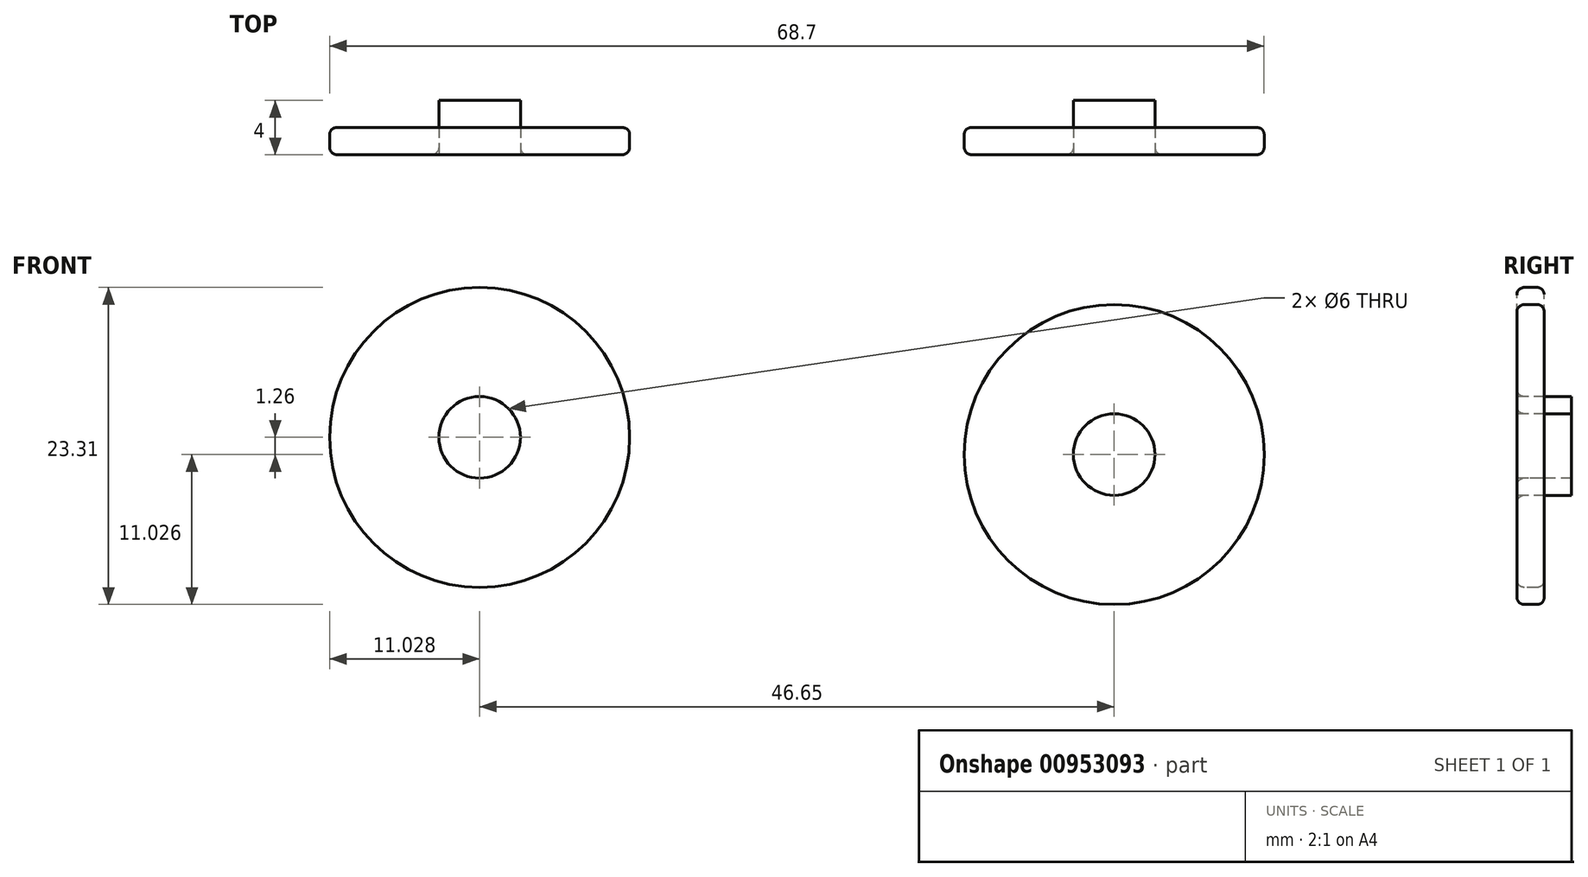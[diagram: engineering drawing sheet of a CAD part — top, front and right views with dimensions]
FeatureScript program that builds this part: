
annotation { "Feature Type Name" : "Feature", "Feature Type Description" : "" }
export const myFeature = defineFeature(function(context is Context, id is Id, definition is map)
    precondition{}
    {
        {
            var Q0;
            Q0=qCreatedBy(makeId("Front.planeOp"),FACE);
            var sketch = newSketch(context, id + "F0", { "sketchPlane" : qUnion([Q0])});
            skCircle(sketch, "E0", {"center": v(-66.5, 54.88) * mm, "radius": 11.03 * mm});
            skCircle(sketch, "E1", {"center": v(-19.84, 53.62) * mm, "radius": 11.03 * mm});
            skCircle(sketch, "E2", {"center": v(-66.5, 54.88) * mm, "radius": 3 * mm});
            skCircle(sketch, "E3", {"center": v(-19.84, 53.62) * mm, "radius": 3 * mm});
            skSolve(sketch);
        }
        {
            var Q0;
            Q0=makeQuery(id+"F0.imprint","IMPRINT",FACE,{"disambiguationData":[TD([[makeQuery(id+"F0.imprint","IMPRINT",EDGE,{"derivedFrom":sQuery(id+"F0.wireOp",EDGE,"E1")}),1.0]])]});
            var Q1;
            Q1=makeQuery(id+"F0.imprint","IMPRINT",FACE,{"disambiguationData":[TD([[makeQuery(id+"F0.imprint","IMPRINT",EDGE,{"derivedFrom":sQuery(id+"F0.wireOp",EDGE,"E0")}),1.0]])]});
            extrude(context, id + "F1", {"entities" : qUnion([Q0, Q1]), "depth" : -2 * mm, "offsetDistance" : 25.4 * mm});
        }
        {
            var Q0;
            Q0=makeQuery(id+"F1.opExtrude","CAP_EDGE",EDGE,{"disambiguationData":[OSD([sQuery(id+"F0.wireOp",EDGE,"E1")])],"isStart":false});
            var Q1;
            Q1=makeQuery(id+"F1.opExtrude","CAP_EDGE",EDGE,{"disambiguationData":[OSD([sQuery(id+"F0.wireOp",EDGE,"E0")])],"isStart":false});
            fillet(context, id + "F2", {"entities" : qUnion([Q0, Q1]), "radius" : .5 * mm, "tangentPropagation" : true, "allowEdgeOverflow" : false});
        }
        {
            var Q0;
            Q0=makeQuery(id+"F0.imprint","IMPRINT",FACE,{"disambiguationData":[TD([[makeQuery(id+"F0.imprint","IMPRINT",EDGE,{"derivedFrom":sQuery(id+"F0.wireOp",EDGE,"E2")}),1.0]])]});
            var Q1;
            Q1=makeQuery(id+"F0.imprint","IMPRINT",FACE,{"disambiguationData":[TD([[makeQuery(id+"F0.imprint","IMPRINT",EDGE,{"derivedFrom":sQuery(id+"F0.wireOp",EDGE,"E3")}),1.0]])]});
            extrude(context, id + "F3", {"entities" : qUnion([Q0, Q1]), "depth" : -4 * mm, "offsetDistance" : 25.4 * mm});
        }
        {
            var Q0;
            Q0=makeQuery(id+"F1.opExtrude","CAP_FACE",FACE,{"disambiguationData":[OSD([sQuery(id+"F0.wireOp",EDGE,"E0"),sQuery(id+"F0.wireOp",EDGE,"E2")])],"isStart":true});
            var Q1;
            Q1=makeQuery(id+"F1.opExtrude","CAP_FACE",FACE,{"disambiguationData":[OSD([sQuery(id+"F0.wireOp",EDGE,"E1"),sQuery(id+"F0.wireOp",EDGE,"E3")])],"isStart":true});
            fillet(context, id + "F4", {"entities" : qUnion([Q0, Q1]), "radius" : .55 * mm, "tangentPropagation" : true, "allowEdgeOverflow" : false});
        }
    });
